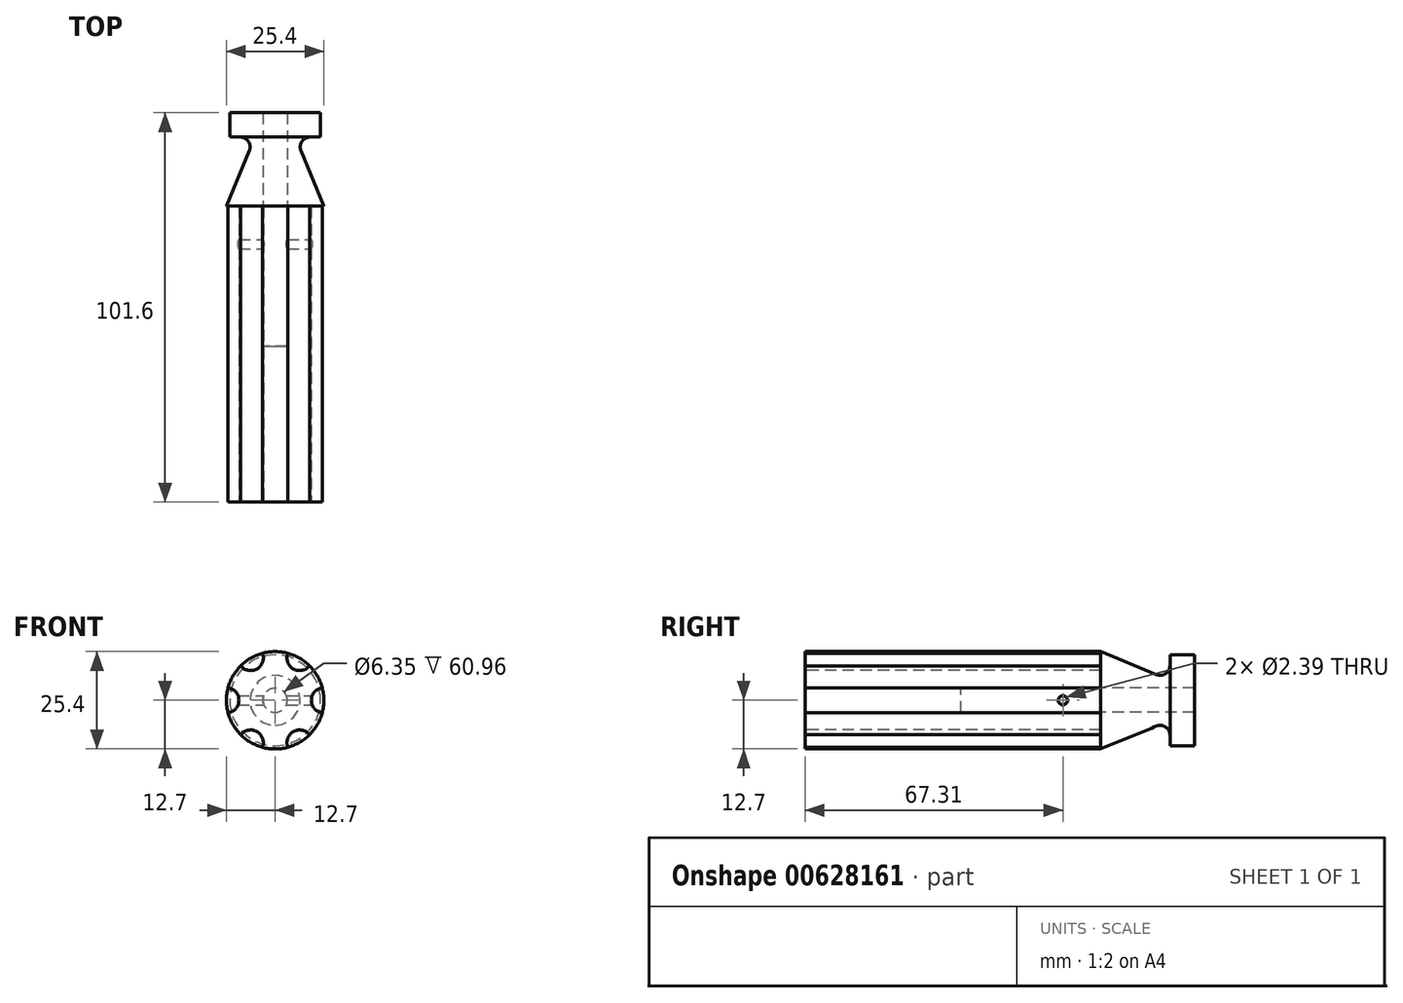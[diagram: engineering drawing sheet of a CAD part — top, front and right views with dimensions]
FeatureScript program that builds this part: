
annotation { "Feature Type Name" : "Feature", "Feature Type Description" : "" }
export const myFeature = defineFeature(function(context is Context, id is Id, definition is map)
    precondition{}
    {
        {
            var Q0;
            Q0=qCreatedBy(makeId("Right.planeOp"),FACE);
            var sketch = newSketch(context, id + "F0", { "sketchPlane" : qUnion([Q0])});
            skLineSegment(sketch, "E0", {"start": v(0, 0) * mm, "end": v(101.6, 0) * mm});
            skLineSegment(sketch, "E1", {"start": v(101.6, 0) * mm, "end": v(101.6, 11.86) * mm});
            skLineSegment(sketch, "E2", {"start": v(77.22, 12.7) * mm, "end": v(0, 12.7) * mm});
            skLineSegment(sketch, "E3", {"start": v(0, 12.7) * mm, "end": v(0, 0) * mm});
            skLineSegment(sketch, "E4", {"start": v(101.6, 11.86) * mm, "end": v(95.25, 11.86) * mm});
            skLineSegment(sketch, "E5", {"start": v(95.25, 11.86) * mm, "end": v(95.25, 9.06) * mm});
            skLineSegment(sketch, "E6", {"start": v(77.22, 12.7) * mm, "end": v(91.76, 6.72) * mm});
            skPoint(sketch, "E7.visualSharp", {"position": v(95.25, 5.3) * mm});
            skArc(sketch, "E7.filletArc", {"start": v(91.76, 6.72) * mm, "mid": v(94.13, 6.96) * mm, "end": v(95.25, 9.06) * mm});
            skSolve(sketch);
        }
        {
            var Q0;
            Q0=makeQuery(id+"F0.imprint","IMPRINT",FACE,{"disambiguationData":[TD([[makeQuery(id+"F0.imprint","IMPRINT",EDGE,{"derivedFrom":sQuery(id+"F0.wireOp",EDGE,"9OTETnfe-vp76-fOas-uP0b-dxW3osHoxaMp")}),1.0]])]});
            var Q1;
            Q1=makeQuery(id+"F0.imprint","IMPRINT",FACE,{"disambiguationData":[TD([[makeQuery(id+"F0.imprint","IMPRINT",EDGE,{"derivedFrom":sQuery(id+"F0.wireOp",EDGE,"E0")}),1.0]])]});
            var Q2;
            Q2=sQuery(id+"F0.wireOp",EDGE,"E0");
            revolve(context, id + "F1", {"entities" : qUnion([Q0, Q1]), "axis" : qUnion([Q2]), "revolveType" : RevolveType.FULL});
        }
        {
            var Q0;
            Q0=qCreatedBy(makeId("Front.planeOp"),FACE);
            var sketch = newSketch(context, id + "F2", { "sketchPlane" : qUnion([Q0])});
            skCircle(sketch, "E8", {"center": v(12.76, 0) * mm, "radius": 3.3 * mm});
            skCircle(sketch, "E9.1.0", {"center": v(6.38, 11.05) * mm, "radius": 3.3 * mm});
            skCircle(sketch, "E9.2.0", {"center": v(-6.38, 11.05) * mm, "radius": 3.3 * mm});
            skCircle(sketch, "E9.3.0", {"center": v(-12.76, 0) * mm, "radius": 3.3 * mm});
            skCircle(sketch, "E9.4.0", {"center": v(-6.38, -11.05) * mm, "radius": 3.3 * mm});
            skCircle(sketch, "E9.5.0", {"center": v(6.38, -11.05) * mm, "radius": 3.3 * mm});
            skPoint(sketch, "E9.center", {"position": v(0, 0) * mm});
            skSolve(sketch);
        }
        {
            var Q0;
            Q0 = qSketchRegion(id + "F2", true);
            extrude(context, id + "F3", {"entities" : qUnion([Q0]), "operationType" : NewBodyOperationType.REMOVE, "oppositeDirection" : true, "depth" : 77.22 * mm, "offsetDistance" : 25.4 * mm});
        }
        {
            var Q0;
            Q0=qCreatedBy(makeId("Front.planeOp"),FACE);
            var sketch = newSketch(context, id + "F4", { "sketchPlane" : qUnion([Q0])});
            skCircle(sketch, "E10", {"center": v(0, 0) * mm, "radius": 3.18 * mm});
            skSolve(sketch);
        }
        {
            var Q0;
            Q0 = qSketchRegion(id + "F4", true);
            extrude(context, id + "F5", {"entities" : qUnion([Q0]), "operationType" : NewBodyOperationType.REMOVE, "endBound" : BoundingType.THROUGH_ALL, "oppositeDirection" : true, "depth" : 40.64 * mm, "offsetDistance" : 25.4 * mm, "hasSecondDirection" : true, "secondDirectionOppositeDirection" : true, "secondDirectionDepth" : 40.64 * mm});
        }
        {
            var Q0;
            Q0=qCreatedBy(makeId("Right.planeOp"),FACE);
            var sketch = newSketch(context, id + "F6", { "sketchPlane" : qUnion([Q0])});
            skCircle(sketch, "E11", {"center": v(67.31, 0) * mm, "radius": 1.2 * mm});
            skSolve(sketch);
        }
        {
            var Q0;
            Q0 = qSketchRegion(id + "F6", true);
            extrude(context, id + "F7", {"entities" : qUnion([Q0]), "operationType" : NewBodyOperationType.REMOVE, "oppositeDirection" : true, "depth" : 25.4 * mm, "offsetDistance" : 25.4 * mm, "hasSecondDirection" : true, "secondDirectionOppositeDirection" : false, "secondDirectionDepth" : 25.4 * mm});
        }
    });
